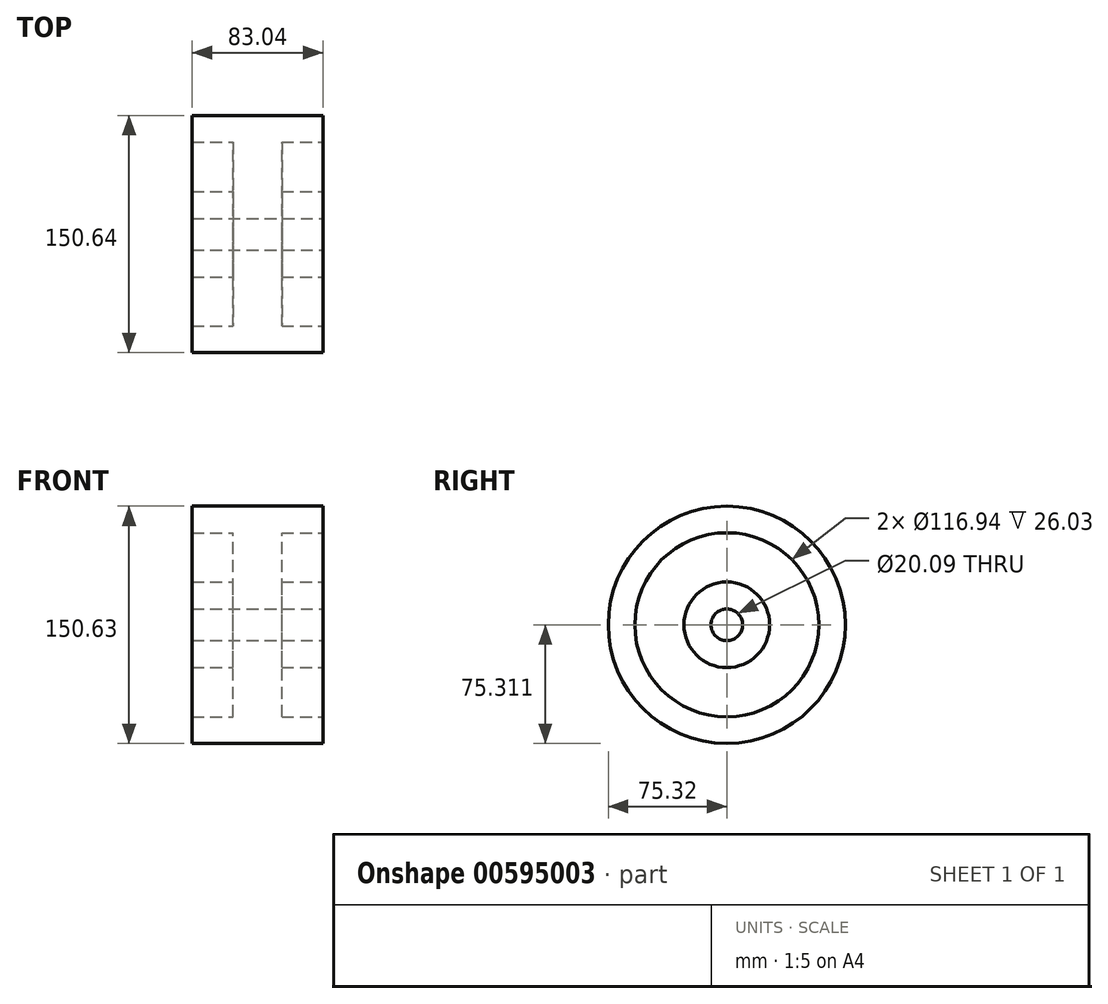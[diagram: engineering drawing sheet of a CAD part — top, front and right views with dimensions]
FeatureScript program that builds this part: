
annotation { "Feature Type Name" : "Feature", "Feature Type Description" : "" }
export const myFeature = defineFeature(function(context is Context, id is Id, definition is map)
    precondition{}
    {
        {
            var Q0;
            Q0=qCreatedBy(makeId("Front.planeOp"),FACE);
            var sketch = newSketch(context, id + "F0", { "sketchPlane" : qUnion([Q0])});
            skLineSegment(sketch, "E0", {"start": v(-41.52, 55.8) * mm, "end": v(0, 55.8) * mm});
            skLineSegment(sketch, "E1", {"start": v(-41.52, 56.46) * mm, "end": v(-41.52, 38.95) * mm});
            skLineSegment(sketch, "E2", {"start": v(-41.52, 38.95) * mm, "end": v(-15.5, 38.95) * mm});
            skLineSegment(sketch, "E3", {"start": v(-15.5, 38.95) * mm, "end": v(-15.5, 7.67) * mm});
            skLineSegment(sketch, "E4", {"start": v(-15.5, 7.67) * mm, "end": v(-41.52, 7.67) * mm});
            skLineSegment(sketch, "E5", {"start": v(-41.52, 7.67) * mm, "end": v(-41.52, -9.47) * mm});
            skLineSegment(sketch, "E6", {"start": v(-41.52, -9.47) * mm, "end": v(0, -9.47) * mm});
            skLineSegment(sketch, "E7.MirrorCS", {"start": v(41.52, 55.8) * mm, "end": v(0, 55.8) * mm});
            skLineSegment(sketch, "E8.MirrorCS", {"start": v(41.52, 56.46) * mm, "end": v(41.52, 38.95) * mm});
            skLineSegment(sketch, "E9.MirrorCS", {"start": v(41.52, 38.95) * mm, "end": v(15.5, 38.95) * mm});
            skLineSegment(sketch, "E10.MirrorCS", {"start": v(15.5, 38.95) * mm, "end": v(15.5, 7.67) * mm});
            skLineSegment(sketch, "E11.MirrorCS", {"start": v(15.5, 7.67) * mm, "end": v(41.52, 7.67) * mm});
            skLineSegment(sketch, "E12.MirrorCS", {"start": v(41.52, -9.47) * mm, "end": v(0, -9.47) * mm});
            skLineSegment(sketch, "E13.MirrorCS", {"start": v(41.52, 7.67) * mm, "end": v(41.52, -9.47) * mm});
            skLineSegment(sketch, "E14", {"start": v(76.09, -19.52) * mm, "end": v(-75.56, -19.52) * mm});
            skSolve(sketch);
        }
        {
            var Q0;
            {var subQ3=sQuery(id+"F0.wireOp",EDGE,"E0");Q0=makeQuery(id+"F0.imprint","IMPRINT",FACE,{"disambiguationData":[TD([[makeQuery(id+"F0.imprint","IMPRINT",EDGE,{"derivedFrom":subQ3}),-1.0]])]});}
            var Q1;
            Q1=sQuery(id+"F0.wireOp",EDGE,"E14");
            revolve(context, id + "F1", {"entities" : qUnion([Q0]), "axis" : qUnion([Q1]), "revolveType" : RevolveType.FULL});
        }
    });
